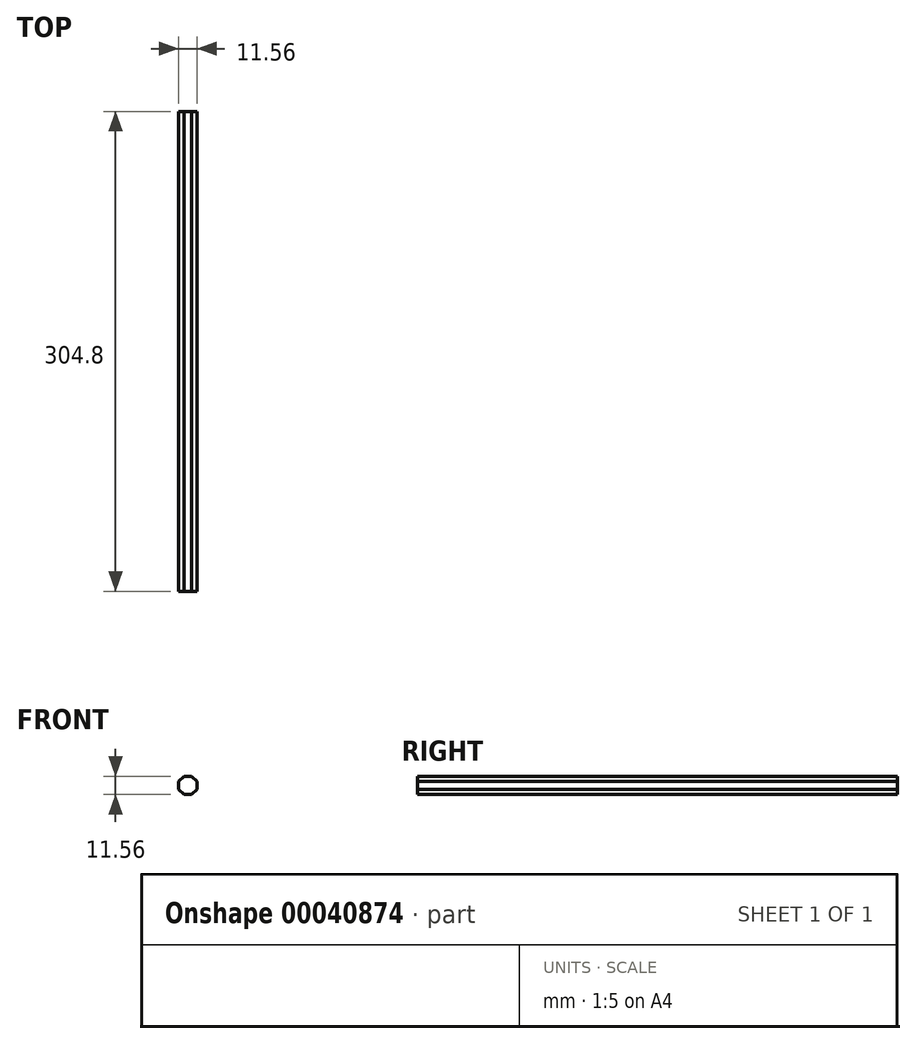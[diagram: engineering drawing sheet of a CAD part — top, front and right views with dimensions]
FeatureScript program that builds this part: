
annotation { "Feature Type Name" : "Feature", "Feature Type Description" : "" }
export const myFeature = defineFeature(function(context is Context, id is Id, definition is map)
    precondition{}
    {
        {
            var Q0;
            Q0=qCreatedBy(makeId("Front.planeOp"),FACE);
            var sketch = newSketch(context, id + "F0", { "sketchPlane" : qUnion([Q0])});
            skCircle(sketch, "E0.cCircle", {"center": v(-45.6, 36.42) * mm, "radius": 5.78 * mm, "construction": true});
            skLineSegment(sketch, "E0.0", {"start": v(-39.81, 38.82) * mm, "end": v(-39.81, 34.03) * mm});
            skLineSegment(sketch, "E0.1", {"start": v(-39.81, 34.03) * mm, "end": v(-43.2, 30.64) * mm});
            skLineSegment(sketch, "E0.2", {"start": v(-43.2, 30.64) * mm, "end": v(-47.99, 30.64) * mm});
            skLineSegment(sketch, "E0.3", {"start": v(-47.99, 30.64) * mm, "end": v(-51.37, 34.03) * mm});
            skLineSegment(sketch, "E0.4", {"start": v(-51.37, 34.03) * mm, "end": v(-51.37, 38.82) * mm});
            skLineSegment(sketch, "E0.5", {"start": v(-51.37, 38.82) * mm, "end": v(-47.99, 42.2) * mm});
            skLineSegment(sketch, "E0.6", {"start": v(-47.99, 42.2) * mm, "end": v(-43.2, 42.2) * mm});
            skLineSegment(sketch, "E0.7", {"start": v(-43.2, 42.2) * mm, "end": v(-39.81, 38.82) * mm});
            skPoint(sketch, "E0.0.midPoint", {"position": v(-39.81, 36.42) * mm});
            skSolve(sketch);
        }
        {
            var Q0;
            Q0 = qSketchRegion(id + "F0", true);
            extrude(context, id + "F1", {"entities" : qUnion([Q0]), "depth" : 304.8 * mm});
        }
    });
